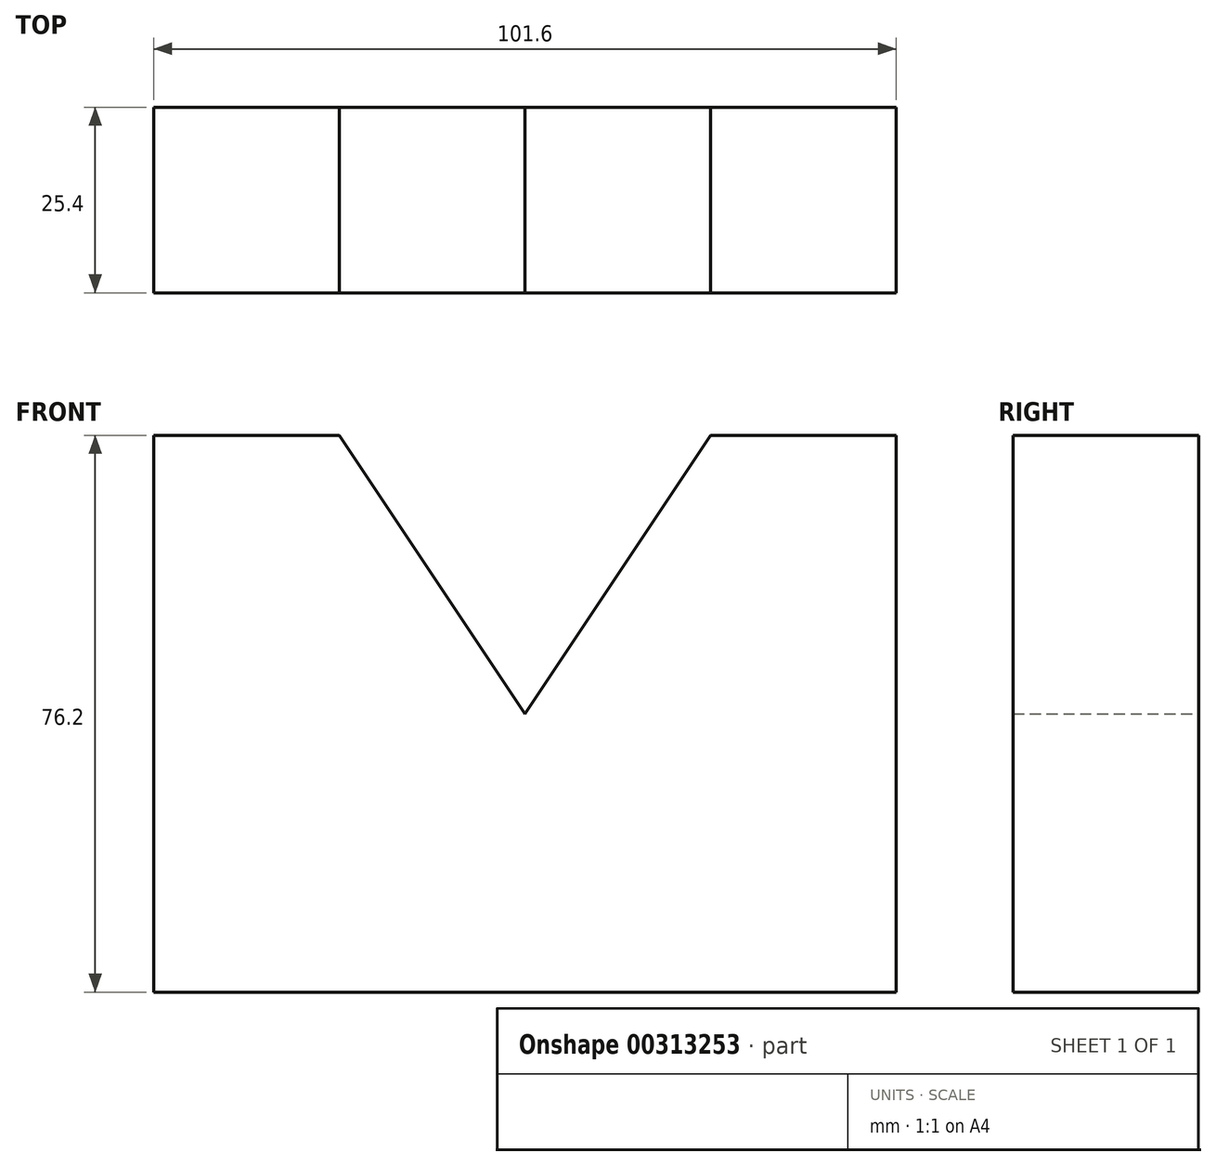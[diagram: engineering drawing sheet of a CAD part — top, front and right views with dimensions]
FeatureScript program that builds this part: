
annotation { "Feature Type Name" : "Feature", "Feature Type Description" : "" }
export const myFeature = defineFeature(function(context is Context, id is Id, definition is map)
    precondition{}
    {
        {
            var Q0;
            Q0=qCreatedBy(makeId("Front.planeOp"),FACE);
            var sketch = newSketch(context, id + "F0", { "sketchPlane" : qUnion([Q0])});
            skLineSegment(sketch, "E0", {"start": v(-53.13, -48.88) * mm, "end": v(48.47, -48.88) * mm});
            skLineSegment(sketch, "E1", {"start": v(48.47, -48.88) * mm, "end": v(48.47, 27.32) * mm});
            skLineSegment(sketch, "E2", {"start": v(48.47, 27.32) * mm, "end": v(23.07, 27.32) * mm});
            skLineSegment(sketch, "E3", {"start": v(-53.13, -48.88) * mm, "end": v(-53.13, 27.32) * mm});
            skLineSegment(sketch, "E4", {"start": v(-53.13, 27.32) * mm, "end": v(-27.73, 27.32) * mm});
            skLineSegment(sketch, "E5", {"start": v(-27.73, 27.32) * mm, "end": v(-2.33, -10.78) * mm});
            skLineSegment(sketch, "E6", {"start": v(-2.33, -10.78) * mm, "end": v(23.07, 27.32) * mm});
            skSolve(sketch);
        }
        {
            var Q0;
            Q0=makeQuery(id+"F0.imprint","IMPRINT",FACE,{"disambiguationData":[TD([[makeQuery(id+"F0.imprint","IMPRINT",EDGE,{"derivedFrom":sQuery(id+"F0.wireOp",EDGE,"E0")}),1.0]])]});
            extrude(context, id + "F1", {"entities" : qUnion([Q0]), "depth" : 25.4 * mm});
        }
    });
